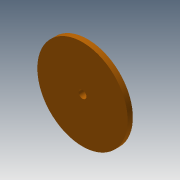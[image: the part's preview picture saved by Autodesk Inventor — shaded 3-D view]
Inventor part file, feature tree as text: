
AUTODESK INVENTOR PART (.ipt)
format: ipt  version: 2013 (Build 170138000, 138)  size: 91,136 bytes
history: native  units: mm
features: extrude x3, sketch x3
ambient origin geometry x8: Origin, YZ Plane, XZ Plane, XY Plane, X Axis, Y Axis, Z Axis, Center Point
bodies: Solid1 (feature_tree)
feature tree (6):
  extrude  "Extrusion1"  Depth=3.0mm
  extrude  "Extrusion2"  Depth=10.0mm
  extrude  "Extrusion3"  Depth=6.0mm
  sketch  "Sketch1"  dims[d0=35.0mm d1=3.0mm]
  sketch  "Sketch2"  dims[d2=2.0mm d3=0.0mm d4=10.0mm]
  sketch  "Sketch3"  dims[d5=3.8mm d6=0.0mm d7=6.0mm d8=3.8mm d9=0.0mm]
